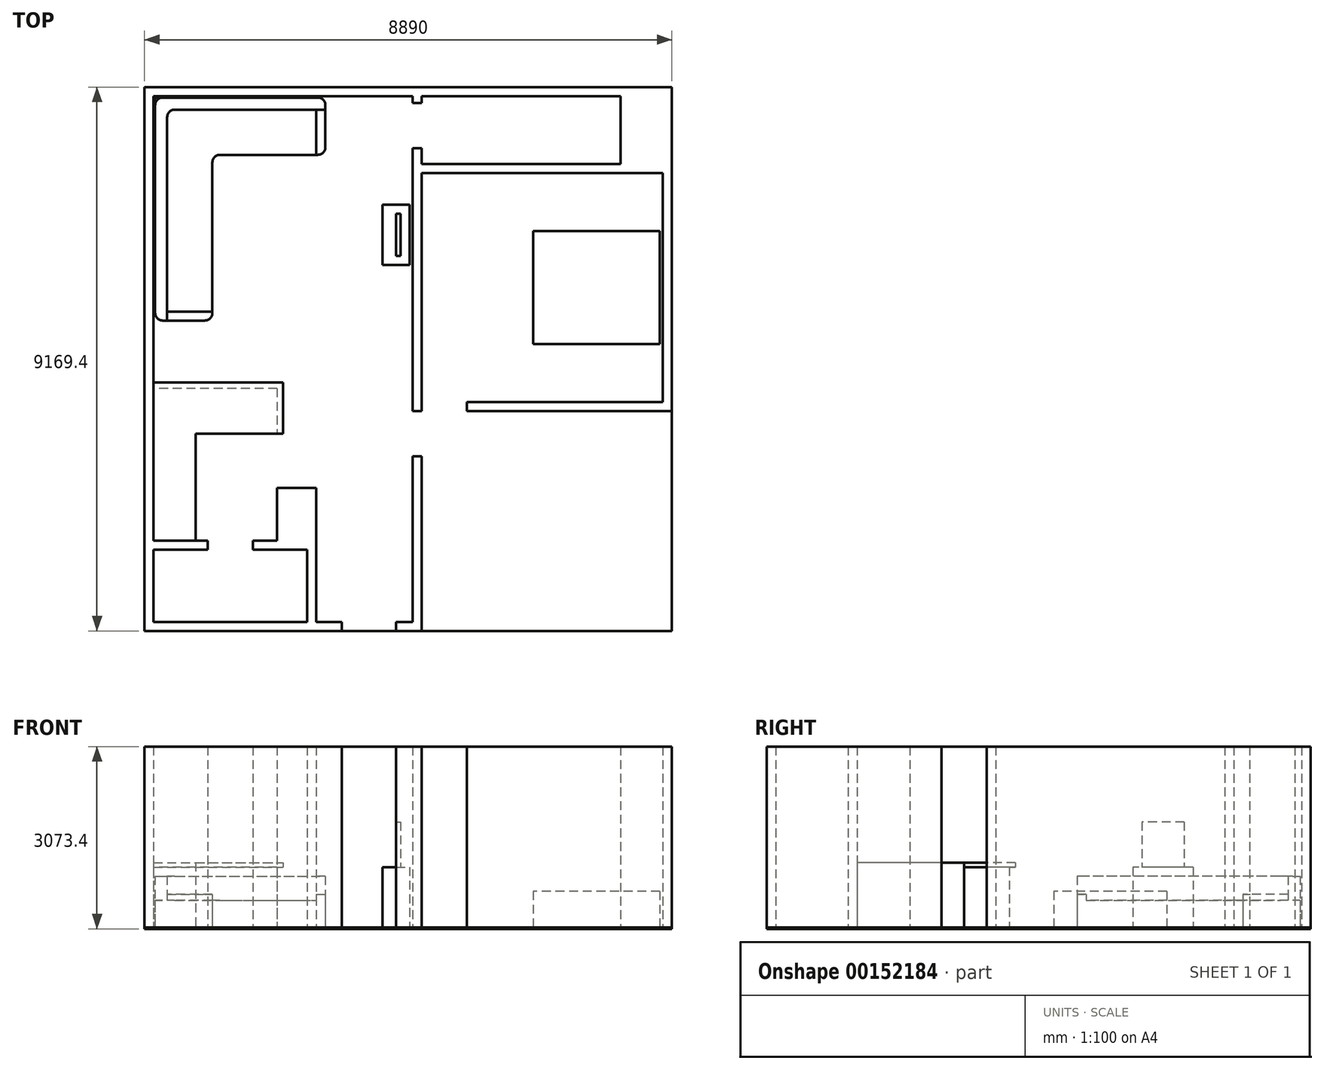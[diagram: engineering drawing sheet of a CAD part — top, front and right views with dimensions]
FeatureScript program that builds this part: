
annotation { "Feature Type Name" : "Feature", "Feature Type Description" : "" }
export const myFeature = defineFeature(function(context is Context, id is Id, definition is map)
    precondition{}
    {
        {
            var Q0;
            Q0=qCreatedBy(makeId("Top.planeOp"),FACE);
            var sketch = newSketch(context, id + "F0", { "sketchPlane" : qUnion([Q0])});
            skLineSegment(sketch, "E0.bottom", {"start": v(-4368.8, 4927.6) * mm, "end": v(0, 4927.6) * mm});
            skLineSegment(sketch, "E0.top", {"start": v(-3657.6, 0) * mm, "end": v(0, 0) * mm, "construction": true});
            skLineSegment(sketch, "E0.left", {"start": v(-4368.8, 4927.6) * mm, "end": v(-4368.8, 152.4) * mm});
            skLineSegment(sketch, "E0.right", {"start": v(0, 4927.6) * mm, "end": v(0, 4813.3) * mm});
            skLineSegment(sketch, "E1.bottom", {"start": v(-2286, 0) * mm, "end": v(-3657.6, 0) * mm});
            skLineSegment(sketch, "E1.top", {"start": v(152.4, 5080) * mm, "end": v(-4521.2, 5080) * mm});
            skLineSegment(sketch, "E1.left", {"start": v(152.4, 0) * mm, "end": v(152.4, 3632.2) * mm});
            skLineSegment(sketch, "E1.right", {"start": v(-4521.2, -6.75) * mm, "end": v(-4521.2, 5080) * mm});
            skLineSegment(sketch, "E2.bottom", {"start": v(-3657.6, 0) * mm, "end": v(-2286, 0) * mm});
            skLineSegment(sketch, "E2.top", {"start": v(-3657.6, -762) * mm, "end": v(-2286, -762) * mm});
            skLineSegment(sketch, "E2.left", {"start": v(-4368.8, 0) * mm, "end": v(-4368.8, -762) * mm});
            skLineSegment(sketch, "E2.right", {"start": v(-2286, 0) * mm, "end": v(-2286, -762) * mm});
            skLineSegment(sketch, "E3.top", {"start": v(-4368.8, -2565.4) * mm, "end": v(-3657.6, -2565.4) * mm});
            skLineSegment(sketch, "E3.left", {"start": v(-4368.8, 0) * mm, "end": v(-4368.8, -2565.4) * mm});
            skLineSegment(sketch, "E3.right", {"start": v(-3657.6, -762) * mm, "end": v(-3657.6, -2565.4) * mm});
            skLineSegment(sketch, "E4.bottom", {"start": v(-4368.8, -2565.4) * mm, "end": v(-3454.4, -2565.4) * mm});
            skLineSegment(sketch, "E4.top", {"start": v(-4368.8, -4089.4) * mm, "end": v(-1625.6, -4089.4) * mm});
            skLineSegment(sketch, "E4.left", {"start": v(-4368.8, -2717.8) * mm, "end": v(-4368.8, -3937) * mm});
            skLineSegment(sketch, "E4.right", {"start": v(-1625.6, -2565.4) * mm, "end": v(-1625.6, -3937) * mm});
            skLineSegment(sketch, "E5.1", {"start": v(-4368.8, -2717.8) * mm, "end": v(-3454.4, -2717.8) * mm});
            skLineSegment(sketch, "E5.2", {"start": v(-1778, -2717.8) * mm, "end": v(-1778, -3937) * mm});
            skLineSegment(sketch, "E5.3", {"start": v(-4368.8, -3937) * mm, "end": v(-1778, -3937) * mm});
            skLineSegment(sketch, "E6", {"start": v(-3073.4, -3937) * mm, "end": v(-3073.4, -3445.39) * mm, "construction": true});
            skLineSegment(sketch, "E7", {"start": v(-3454.4, -2565.4) * mm, "end": v(-3454.4, -2717.8) * mm});
            skLineSegment(sketch, "E8", {"start": v(-2692.4, -2717.8) * mm, "end": v(-2692.4, -2565.4) * mm});
            skLineSegment(sketch, "E9.0", {"start": v(-4521.2, -1866.2) * mm, "end": v(-4521.2, -4089.4) * mm});
            skLineSegment(sketch, "E9.1", {"start": v(-4521.2, 0) * mm, "end": v(-4521.2, -1866.2) * mm});
            skLineSegment(sketch, "E10", {"start": v(-4368.8, -4089.4) * mm, "end": v(-4521.2, -4089.4) * mm});
            skLineSegment(sketch, "E11.right", {"start": v(-2286, 0) * mm, "end": v(-2311.9, 0) * mm});
            skLineSegment(sketch, "E12.bottom", {"start": v(-1625.6, -4089.4) * mm, "end": v(-1193.8, -4089.4) * mm});
            skLineSegment(sketch, "E12.top", {"start": v(-1625.6, -3937) * mm, "end": v(-1193.8, -3937) * mm});
            skLineSegment(sketch, "E12.right", {"start": v(152.4, -4089.4) * mm, "end": v(152.4, -3937) * mm});
            skLineSegment(sketch, "E13.top", {"start": v(152.4, -1143) * mm, "end": v(0, -1143) * mm});
            skLineSegment(sketch, "E13.left", {"start": v(152.4, -3937) * mm, "end": v(152.4, -1143) * mm});
            skLineSegment(sketch, "E13.right", {"start": v(0, -3937) * mm, "end": v(0, -1143) * mm});
            skLineSegment(sketch, "E14.top", {"start": v(0, -381) * mm, "end": v(152.4, -381) * mm});
            skLineSegment(sketch, "E14.left", {"start": v(0, 0) * mm, "end": v(0, -381) * mm});
            skLineSegment(sketch, "E14.right", {"start": v(152.4, 0) * mm, "end": v(152.4, -381) * mm});
            skLineSegment(sketch, "E15.bottom", {"start": v(152.4, 5080) * mm, "end": v(3505.2, 5080) * mm});
            skLineSegment(sketch, "E15.top", {"start": v(152.4, 4927.6) * mm, "end": v(3505.2, 4927.6) * mm});
            skLineSegment(sketch, "E16.bottom", {"start": v(3505.2, 5080) * mm, "end": v(4368.8, 5080) * mm});
            skLineSegment(sketch, "E16.left", {"start": v(3505.2, 4927.6) * mm, "end": v(3505.2, 3784.6) * mm});
            skLineSegment(sketch, "E16.right", {"start": v(4368.8, 5080) * mm, "end": v(4368.8, 3784.6) * mm});
            skLineSegment(sketch, "E17.bottom", {"start": v(3505.2, 3784.6) * mm, "end": v(152.4, 3784.6) * mm});
            skLineSegment(sketch, "E17.top", {"start": v(4216.4, 3632.2) * mm, "end": v(152.4, 3632.2) * mm});
            skLineSegment(sketch, "E17.left", {"start": v(4368.8, 3784.6) * mm, "end": v(4368.8, 3632.2) * mm});
            skLineSegment(sketch, "E18.top", {"start": v(4368.8, -381) * mm, "end": v(4216.4, -381) * mm});
            skLineSegment(sketch, "E18.left", {"start": v(4368.8, 3632.2) * mm, "end": v(4368.8, -381) * mm});
            skLineSegment(sketch, "E18.right", {"start": v(4216.4, 3632.2) * mm, "end": v(4216.4, -228.6) * mm});
            skLineSegment(sketch, "E19.bottom", {"start": v(4216.4, -381) * mm, "end": v(914.4, -381) * mm});
            skLineSegment(sketch, "E19.top", {"start": v(4216.4, -228.6) * mm, "end": v(914.4, -228.6) * mm});
            skLineSegment(sketch, "E19.right", {"start": v(914.4, -381) * mm, "end": v(914.4, -228.6) * mm});
            skLineSegment(sketch, "E20.bottom", {"start": v(0, 4813.3) * mm, "end": v(152.4, 4813.3) * mm});
            skLineSegment(sketch, "E20.top", {"start": v(0, 4051.3) * mm, "end": v(152.4, 4051.3) * mm});
            skLineSegment(sketch, "E21", {"start": v(3505.2, 4432.3) * mm, "end": v(2543.45, 4432.3) * mm, "construction": true});
            skLineSegment(sketch, "E22.trimOffspring", {"start": v(152.4, 3784.6) * mm, "end": v(152.4, 4051.3) * mm});
            skLineSegment(sketch, "E23.trimOffspring", {"start": v(152.4, 4813.3) * mm, "end": v(152.4, 4927.6) * mm});
            skLineSegment(sketch, "E24.trimOffspring", {"start": v(0, 4051.3) * mm, "end": v(0, 0) * mm});
            skLineSegment(sketch, "E25", {"start": v(-4368.8, 0) * mm, "end": v(-3657.6, 0) * mm});
            skLineSegment(sketch, "E26", {"start": v(-4368.8, 0) * mm, "end": v(-4368.8, 152.4) * mm});
            skLineSegment(sketch, "E27.trimOffspring", {"start": v(-2692.4, -2565.4) * mm, "end": v(-2286, -2565.4) * mm});
            skLineSegment(sketch, "E28.trimOffspring", {"start": v(-2692.4, -2717.8) * mm, "end": v(-1778, -2717.8) * mm});
            skLineSegment(sketch, "E29", {"start": v(-736.6, -4089.4) * mm, "end": v(-736.6, -3937) * mm, "construction": true});
            skLineSegment(sketch, "E30.left", {"start": v(-1193.8, -4089.4) * mm, "end": v(-1193.8, -3937) * mm});
            skLineSegment(sketch, "E30.right", {"start": v(-279.4, -4089.4) * mm, "end": v(-279.4, -3937) * mm});
            skLineSegment(sketch, "E31.trimOffspring", {"start": v(-279.4, -4089.4) * mm, "end": v(152.4, -4089.4) * mm});
            skLineSegment(sketch, "E32.trimOffspring", {"start": v(-279.4, -3937) * mm, "end": v(0, -3937) * mm});
            skLineSegment(sketch, "E33.top", {"start": v(-1625.6, -1676.4) * mm, "end": v(-2286, -1676.4) * mm});
            skLineSegment(sketch, "E33.left", {"start": v(-1625.6, -2565.4) * mm, "end": v(-1625.6, -1676.4) * mm});
            skLineSegment(sketch, "E33.right", {"start": v(-2286, -2565.4) * mm, "end": v(-2286, -1676.4) * mm});
            skSolve(sketch);
        }
        {
            var Q0;
            Q0 = qSketchRegion(id + "F0", true);
            extrude(context, id + "F1", {"entities" : qUnion([Q0]), "depth" : 1016 * mm});
        }
        {
            var Q0;
            Q0=makeQuery(id+"F1.opExtrude","CAP_FACE",FACE,{"disambiguationData":[OSD([sQuery(id+"F0.wireOp",EDGE,"E0.bottom"),sQuery(id+"F0.wireOp",EDGE,"E0.left"),sQuery(id+"F0.wireOp",EDGE,"E0.right"),sQuery(id+"F0.wireOp",EDGE,"E1.top"),sQuery(id+"F0.wireOp",EDGE,"E1.left"),sQuery(id+"F0.wireOp",EDGE,"E1.right"),sQuery(id+"F0.wireOp",EDGE,"E2.top"),sQuery(id+"F0.wireOp",EDGE,"E2.right"),sQuery(id+"F0.wireOp",EDGE,"E3.right"),sQuery(id+"F0.wireOp",EDGE,"E4.bottom"),sQuery(id+"F0.wireOp",EDGE,"E4.top"),sQuery(id+"F0.wireOp",EDGE,"E4.left"),sQuery(id+"F0.wireOp",EDGE,"E4.right"),sQuery(id+"F0.wireOp",EDGE,"E5.1"),sQuery(id+"F0.wireOp",EDGE,"E5.2"),sQuery(id+"F0.wireOp",EDGE,"E5.3"),sQuery(id+"F0.wireOp",EDGE,"E7"),sQuery(id+"F0.wireOp",EDGE,"E8"),sQuery(id+"F0.wireOp",EDGE,"E9.0"),sQuery(id+"F0.wireOp",EDGE,"E9.1"),sQuery(id+"F0.wireOp",EDGE,"E10"),sQuery(id+"F0.wireOp",EDGE,"E12.bottom"),sQuery(id+"F0.wireOp",EDGE,"E12.top"),sQuery(id+"F0.wireOp",EDGE,"E14.top"),sQuery(id+"F0.wireOp",EDGE,"E14.left"),sQuery(id+"F0.wireOp",EDGE,"E14.right"),sQuery(id+"F0.wireOp",EDGE,"E15.bottom"),sQuery(id+"F0.wireOp",EDGE,"E15.top"),sQuery(id+"F0.wireOp",EDGE,"E16.bottom"),sQuery(id+"F0.wireOp",EDGE,"E16.left"),sQuery(id+"F0.wireOp",EDGE,"E16.right"),sQuery(id+"F0.wireOp",EDGE,"E17.bottom"),sQuery(id+"F0.wireOp",EDGE,"E17.top"),sQuery(id+"F0.wireOp",EDGE,"E17.left"),sQuery(id+"F0.wireOp",EDGE,"E18.top"),sQuery(id+"F0.wireOp",EDGE,"E18.left"),sQuery(id+"F0.wireOp",EDGE,"E18.right"),sQuery(id+"F0.wireOp",EDGE,"E19.bottom"),sQuery(id+"F0.wireOp",EDGE,"E19.top"),sQuery(id+"F0.wireOp",EDGE,"E19.right"),sQuery(id+"F0.wireOp",EDGE,"E20.bottom"),sQuery(id+"F0.wireOp",EDGE,"E20.top"),sQuery(id+"F0.wireOp",EDGE,"E22.trimOffspring"),sQuery(id+"F0.wireOp",EDGE,"E23.trimOffspring"),sQuery(id+"F0.wireOp",EDGE,"E24.trimOffspring"),sQuery(id+"F0.wireOp",EDGE,"E1.bottom"),sQuery(id+"F0.wireOp",EDGE,"E25"),sQuery(id+"F0.wireOp",EDGE,"E26"),sQuery(id+"F0.wireOp",EDGE,"E27.trimOffspring"),sQuery(id+"F0.wireOp",EDGE,"E28.trimOffspring"),sQuery(id+"F0.wireOp",EDGE,"E30.left"),sQuery(id+"F0.wireOp",EDGE,"E33.top"),sQuery(id+"F0.wireOp",EDGE,"E33.left"),sQuery(id+"F0.wireOp",EDGE,"E33.right")])],"isStart":false});
            var sketch = newSketch(context, id + "F2", { "sketchPlane" : qUnion([Q0])});
            skLineSegment(sketch, "E34.0", {"start": v(-2286, 0) * mm, "end": v(-2286, -762) * mm});
            skLineSegment(sketch, "E34.1", {"start": v(-3657.6, -762) * mm, "end": v(-2286, -762) * mm});
            skLineSegment(sketch, "E34.2", {"start": v(-3657.6, -762) * mm, "end": v(-3657.6, -2565.4) * mm});
            skLineSegment(sketch, "E35.0", {"start": v(-3657.6, -2565.4) * mm, "end": v(-3454.4, -2565.4) * mm});
            skLineSegment(sketch, "E35.1", {"start": v(-1625.6, -1676.4) * mm, "end": v(-1625.6, -3937) * mm});
            skLineSegment(sketch, "E35.2", {"start": v(-1625.6, -1676.4) * mm, "end": v(-2286, -1676.4) * mm});
            skLineSegment(sketch, "E35.3", {"start": v(-2286, -2565.4) * mm, "end": v(-2286, -1676.4) * mm});
            skLineSegment(sketch, "E35.4", {"start": v(-2692.4, -2565.4) * mm, "end": v(-2286, -2565.4) * mm});
            skLineSegment(sketch, "E35.5", {"start": v(-2692.4, -2717.8) * mm, "end": v(-1778, -2717.8) * mm});
            skLineSegment(sketch, "E35.6", {"start": v(-1778, -2717.8) * mm, "end": v(-1778, -3937) * mm});
            skLineSegment(sketch, "E35.7", {"start": v(-4368.8, -3937) * mm, "end": v(-1778, -3937) * mm});
            skLineSegment(sketch, "E35.8", {"start": v(-1625.6, -3937) * mm, "end": v(-1193.8, -3937) * mm});
            skLineSegment(sketch, "E35.9", {"start": v(-1193.8, -4089.4) * mm, "end": v(-4521.2, -4089.4) * mm});
            skLineSegment(sketch, "E35.10", {"start": v(-4368.8, -2717.8) * mm, "end": v(-4368.8, -3937) * mm});
            skLineSegment(sketch, "E35.11", {"start": v(-4521.2, -4089.4) * mm, "end": v(-4521.2, 5080) * mm});
            skLineSegment(sketch, "E35.12", {"start": v(-4368.8, -2717.8) * mm, "end": v(-3454.4, -2717.8) * mm});
            skLineSegment(sketch, "E35.13", {"start": v(-4368.8, 4927.6) * mm, "end": v(-4368.8, 101.6) * mm});
            skLineSegment(sketch, "E35.14", {"start": v(0, -3937) * mm, "end": v(0, -1143) * mm});
            skLineSegment(sketch, "E35.15", {"start": v(152.4, -4089.4) * mm, "end": v(152.4, -1143) * mm});
            skLineSegment(sketch, "E35.16", {"start": v(-279.4, -4089.4) * mm, "end": v(152.4, -4089.4) * mm});
            skLineSegment(sketch, "E35.17", {"start": v(-279.4, -3937) * mm, "end": v(0, -3937) * mm});
            skLineSegment(sketch, "E35.18", {"start": v(152.4, 3632.2) * mm, "end": v(152.4, -381) * mm});
            skLineSegment(sketch, "E35.19", {"start": v(0, 4051.3) * mm, "end": v(0, -381) * mm});
            skLineSegment(sketch, "E35.20", {"start": v(4368.8, -381) * mm, "end": v(914.4, -381) * mm});
            skLineSegment(sketch, "E35.21", {"start": v(4216.4, -228.6) * mm, "end": v(914.4, -228.6) * mm});
            skLineSegment(sketch, "E35.22", {"start": v(914.4, -381) * mm, "end": v(914.4, -228.6) * mm});
            skLineSegment(sketch, "E35.23", {"start": v(0, -381) * mm, "end": v(152.4, -381) * mm});
            skLineSegment(sketch, "E35.24", {"start": v(152.4, -1143) * mm, "end": v(0, -1143) * mm});
            skLineSegment(sketch, "E35.25", {"start": v(-279.4, -4089.4) * mm, "end": v(-279.4, -3937) * mm});
            skLineSegment(sketch, "E35.26", {"start": v(-1193.8, -4089.4) * mm, "end": v(-1193.8, -3937) * mm});
            skLineSegment(sketch, "E35.27", {"start": v(-2692.4, -2717.8) * mm, "end": v(-2692.4, -2565.4) * mm});
            skLineSegment(sketch, "E35.28", {"start": v(-3454.4, -2565.4) * mm, "end": v(-3454.4, -2717.8) * mm});
            skLineSegment(sketch, "E35.29", {"start": v(-4521.2, 5080) * mm, "end": v(4368.8, 5080) * mm});
            skLineSegment(sketch, "E35.30", {"start": v(-4368.8, 4927.6) * mm, "end": v(0, 4927.6) * mm});
            skLineSegment(sketch, "E35.31", {"start": v(4368.8, 5080) * mm, "end": v(4368.8, -381) * mm});
            skLineSegment(sketch, "E35.32", {"start": v(3505.2, 4927.6) * mm, "end": v(3505.2, 3784.6) * mm});
            skLineSegment(sketch, "E35.33", {"start": v(4216.4, 3632.2) * mm, "end": v(152.4, 3632.2) * mm});
            skLineSegment(sketch, "E35.34", {"start": v(4216.4, 3632.2) * mm, "end": v(4216.4, -228.6) * mm});
            skLineSegment(sketch, "E35.35", {"start": v(3505.2, 3784.6) * mm, "end": v(152.4, 3784.6) * mm});
            skLineSegment(sketch, "E35.36", {"start": v(152.4, 3784.6) * mm, "end": v(152.4, 4051.3) * mm});
            skLineSegment(sketch, "E35.37", {"start": v(0, 4051.3) * mm, "end": v(152.4, 4051.3) * mm});
            skLineSegment(sketch, "E35.38", {"start": v(0, 4813.3) * mm, "end": v(152.4, 4813.3) * mm});
            skLineSegment(sketch, "E35.39", {"start": v(152.4, 4813.3) * mm, "end": v(152.4, 4927.6) * mm});
            skLineSegment(sketch, "E35.40", {"start": v(0, 4927.6) * mm, "end": v(0, 4813.3) * mm});
            skLineSegment(sketch, "E35.41", {"start": v(152.4, 4927.6) * mm, "end": v(3505.2, 4927.6) * mm});
            skLineSegment(sketch, "E36", {"start": v(-2286, 101.6) * mm, "end": v(-4368.8, 101.6) * mm});
            skPoint(sketch, "E37.orphan", {"position": v(-4368.8, 0) * mm});
            skLineSegment(sketch, "E38.bottom", {"start": v(-2286, 101.6) * mm, "end": v(-2184.4, 101.6) * mm});
            skLineSegment(sketch, "E38.top", {"start": v(-2286, -762) * mm, "end": v(-2184.4, -762) * mm});
            skLineSegment(sketch, "E38.right", {"start": v(-2184.4, 101.6) * mm, "end": v(-2184.4, -762) * mm});
            skSolve(sketch);
        }
        {
            var Q0;
            Q0=makeQuery(id+"F2.imprint","IMPRINT",FACE,{"disambiguationData":[TD([[makeQuery(id+"F2.imprint","IMPRINT",EDGE,{"derivedFrom":sQuery(id+"F2.wireOp",EDGE,"E34.1")}),1.0]])]});
            var Q1;
            Q1=makeQuery(id+"F2.imprint","IMPRINT",FACE,{"disambiguationData":[TD([[makeQuery(id+"F2.imprint","IMPRINT",EDGE,{"derivedFrom":sQuery(id+"F2.wireOp",EDGE,"E35.14")}),-1.0]])]});
            var Q2;
            {var subQ0=sQuery(id+"F2.wireOp",EDGE,"E36");Q2=makeQuery(id+"F2.imprint","IMPRINT",FACE,{"disambiguationData":[TD([[makeQuery(id+"F2.imprint","IMPRINT",EDGE,{"derivedFrom":subQ0}),1.0]])]});}
            extrude(context, id + "F3", {"entities" : qUnion([Q0, Q1, Q2]), "operationType" : NewBodyOperationType.ADD, "depth" : 76.2 * mm});
        }
        {
            var Q0;
            Q0=makeQuery(id+"F3.opExtrude","CAP_FACE",FACE,{"disambiguationData":[OSD([sQuery(id+"F2.wireOp",EDGE,"E34.1"),sQuery(id+"F2.wireOp",EDGE,"E34.2"),sQuery(id+"F2.wireOp",EDGE,"E35.0"),sQuery(id+"F2.wireOp",EDGE,"E35.1"),sQuery(id+"F2.wireOp",EDGE,"E35.2"),sQuery(id+"F2.wireOp",EDGE,"E35.3"),sQuery(id+"F2.wireOp",EDGE,"E35.4"),sQuery(id+"F2.wireOp",EDGE,"E35.5"),sQuery(id+"F2.wireOp",EDGE,"E35.6"),sQuery(id+"F2.wireOp",EDGE,"E35.7"),sQuery(id+"F2.wireOp",EDGE,"E35.8"),sQuery(id+"F2.wireOp",EDGE,"E35.9"),sQuery(id+"F2.wireOp",EDGE,"E35.10"),sQuery(id+"F2.wireOp",EDGE,"E35.11"),sQuery(id+"F2.wireOp",EDGE,"E35.12"),sQuery(id+"F2.wireOp",EDGE,"E35.13"),sQuery(id+"F2.wireOp",EDGE,"E35.18"),sQuery(id+"F2.wireOp",EDGE,"E35.19"),sQuery(id+"F2.wireOp",EDGE,"E35.20"),sQuery(id+"F2.wireOp",EDGE,"E35.21"),sQuery(id+"F2.wireOp",EDGE,"E35.22"),sQuery(id+"F2.wireOp",EDGE,"E35.23"),sQuery(id+"F2.wireOp",EDGE,"E35.26"),sQuery(id+"F2.wireOp",EDGE,"E35.27"),sQuery(id+"F2.wireOp",EDGE,"E35.28"),sQuery(id+"F2.wireOp",EDGE,"E35.29"),sQuery(id+"F2.wireOp",EDGE,"E35.30"),sQuery(id+"F2.wireOp",EDGE,"E35.31"),sQuery(id+"F2.wireOp",EDGE,"E35.32"),sQuery(id+"F2.wireOp",EDGE,"E35.33"),sQuery(id+"F2.wireOp",EDGE,"E35.34"),sQuery(id+"F2.wireOp",EDGE,"E35.35"),sQuery(id+"F2.wireOp",EDGE,"E35.36"),sQuery(id+"F2.wireOp",EDGE,"E35.37"),sQuery(id+"F2.wireOp",EDGE,"E35.38"),sQuery(id+"F2.wireOp",EDGE,"E35.39"),sQuery(id+"F2.wireOp",EDGE,"E35.40"),sQuery(id+"F2.wireOp",EDGE,"E35.41"),sQuery(id+"F2.wireOp",EDGE,"E36"),sQuery(id+"F2.wireOp",EDGE,"E38.bottom"),sQuery(id+"F2.wireOp",EDGE,"E38.top"),sQuery(id+"F2.wireOp",EDGE,"E38.right")])],"isStart":false});
            var sketch = newSketch(context, id + "F4", { "sketchPlane" : qUnion([Q0])});
            skLineSegment(sketch, "E39.3", {"start": v(-3657.6, -2565.4) * mm, "end": v(-3454.4, -2565.4) * mm});
            skLineSegment(sketch, "E39.4", {"start": v(-1625.6, -1676.4) * mm, "end": v(-1625.6, -3937) * mm});
            skLineSegment(sketch, "E39.5", {"start": v(-1625.6, -1676.4) * mm, "end": v(-2286, -1676.4) * mm});
            skLineSegment(sketch, "E39.6", {"start": v(-2286, -2565.4) * mm, "end": v(-2286, -1676.4) * mm});
            skLineSegment(sketch, "E39.7", {"start": v(-2692.4, -2565.4) * mm, "end": v(-2286, -2565.4) * mm});
            skLineSegment(sketch, "E39.8", {"start": v(-2692.4, -2717.8) * mm, "end": v(-1778, -2717.8) * mm});
            skLineSegment(sketch, "E39.9", {"start": v(-1778, -2717.8) * mm, "end": v(-1778, -3937) * mm});
            skLineSegment(sketch, "E39.10", {"start": v(-4368.8, -3937) * mm, "end": v(-1778, -3937) * mm});
            skLineSegment(sketch, "E39.11", {"start": v(-1625.6, -3937) * mm, "end": v(-1193.8, -3937) * mm});
            skLineSegment(sketch, "E39.12", {"start": v(-1193.8, -4089.4) * mm, "end": v(-4521.2, -4089.4) * mm});
            skLineSegment(sketch, "E39.13", {"start": v(-4368.8, -2717.8) * mm, "end": v(-4368.8, -3937) * mm});
            skLineSegment(sketch, "E39.14", {"start": v(-4521.2, -4089.4) * mm, "end": v(-4521.2, 5080) * mm});
            skLineSegment(sketch, "E39.15", {"start": v(-4368.8, -2717.8) * mm, "end": v(-3454.4, -2717.8) * mm});
            skLineSegment(sketch, "E39.16", {"start": v(-4368.8, 4927.6) * mm, "end": v(-4368.8, 101.6) * mm});
            skLineSegment(sketch, "E39.17", {"start": v(0, -3937) * mm, "end": v(0, -1143) * mm});
            skLineSegment(sketch, "E39.18", {"start": v(152.4, -4089.4) * mm, "end": v(152.4, -1143) * mm});
            skLineSegment(sketch, "E39.19", {"start": v(-279.4, -4089.4) * mm, "end": v(152.4, -4089.4) * mm});
            skLineSegment(sketch, "E39.20", {"start": v(-279.4, -3937) * mm, "end": v(0, -3937) * mm});
            skLineSegment(sketch, "E39.21", {"start": v(152.4, 3632.2) * mm, "end": v(152.4, -381) * mm});
            skLineSegment(sketch, "E39.22", {"start": v(0, 4051.3) * mm, "end": v(0, -381) * mm});
            skLineSegment(sketch, "E39.23", {"start": v(4368.8, -381) * mm, "end": v(914.4, -381) * mm});
            skLineSegment(sketch, "E39.24", {"start": v(4216.4, -228.6) * mm, "end": v(914.4, -228.6) * mm});
            skLineSegment(sketch, "E39.25", {"start": v(914.4, -381) * mm, "end": v(914.4, -228.6) * mm});
            skLineSegment(sketch, "E39.26", {"start": v(0, -381) * mm, "end": v(152.4, -381) * mm});
            skLineSegment(sketch, "E39.27", {"start": v(152.4, -1143) * mm, "end": v(0, -1143) * mm});
            skLineSegment(sketch, "E39.28", {"start": v(-279.4, -4089.4) * mm, "end": v(-279.4, -3937) * mm});
            skLineSegment(sketch, "E39.29", {"start": v(-1193.8, -4089.4) * mm, "end": v(-1193.8, -3937) * mm});
            skLineSegment(sketch, "E39.30", {"start": v(-2692.4, -2717.8) * mm, "end": v(-2692.4, -2565.4) * mm});
            skLineSegment(sketch, "E39.31", {"start": v(-3454.4, -2565.4) * mm, "end": v(-3454.4, -2717.8) * mm});
            skLineSegment(sketch, "E39.32", {"start": v(-4521.2, 5080) * mm, "end": v(4368.8, 5080) * mm});
            skLineSegment(sketch, "E39.33", {"start": v(-4368.8, 4927.6) * mm, "end": v(0, 4927.6) * mm});
            skLineSegment(sketch, "E39.34", {"start": v(4368.8, 5080) * mm, "end": v(4368.8, -381) * mm});
            skLineSegment(sketch, "E39.35", {"start": v(3505.2, 4927.6) * mm, "end": v(3505.2, 3784.6) * mm});
            skLineSegment(sketch, "E39.36", {"start": v(4216.4, 3632.2) * mm, "end": v(152.4, 3632.2) * mm});
            skLineSegment(sketch, "E39.37", {"start": v(4216.4, 3632.2) * mm, "end": v(4216.4, -228.6) * mm});
            skLineSegment(sketch, "E39.38", {"start": v(3505.2, 3784.6) * mm, "end": v(152.4, 3784.6) * mm});
            skLineSegment(sketch, "E39.39", {"start": v(152.4, 3784.6) * mm, "end": v(152.4, 4051.3) * mm});
            skLineSegment(sketch, "E39.40", {"start": v(0, 4051.3) * mm, "end": v(152.4, 4051.3) * mm});
            skLineSegment(sketch, "E39.41", {"start": v(0, 4813.3) * mm, "end": v(152.4, 4813.3) * mm});
            skLineSegment(sketch, "E39.42", {"start": v(152.4, 4813.3) * mm, "end": v(152.4, 4927.6) * mm});
            skLineSegment(sketch, "E39.43", {"start": v(0, 4927.6) * mm, "end": v(0, 4813.3) * mm});
            skLineSegment(sketch, "E39.44", {"start": v(152.4, 4927.6) * mm, "end": v(3505.2, 4927.6) * mm});
            skPoint(sketch, "E39.46", {"position": v(-4368.8, 0) * mm});
            skLineSegment(sketch, "E40", {"start": v(-4368.8, 101.6) * mm, "end": v(-4368.8, -2565.4) * mm});
            skPoint(sketch, "E39.45.end.orphan", {"position": v(-4368.8, 101.6) * mm});
            skPoint(sketch, "E39.2.end.orphan", {"position": v(-3657.6, -2565.4) * mm});
            skLineSegment(sketch, "E41", {"start": v(-3657.6, -2565.4) * mm, "end": v(-4368.8, -2565.4) * mm});
            skSolve(sketch);
        }
        {
            var Q0;
            Q0=makeQuery(id+"F4.imprint","IMPRINT",FACE,{"disambiguationData":[TD([[makeQuery(id+"F4.imprint","IMPRINT",EDGE,{"derivedFrom":sQuery(id+"F4.wireOp",EDGE,"E39.17")}),-1.0]])]});
            var Q1;
            Q1=makeQuery(id+"F4.imprint","IMPRINT",FACE,{"disambiguationData":[TD([[makeQuery(id+"F4.imprint","IMPRINT",EDGE,{"derivedFrom":sQuery(id+"F4.wireOp",EDGE,"E39.3")}),-1.0]])]});
            extrude(context, id + "F5", {"entities" : qUnion([Q0, Q1]), "operationType" : NewBodyOperationType.ADD, "depth" : 1955.8 * mm});
        }
        {
            var Q0;
            Q0=makeQuery(id+"F1.opExtrude","CAP_FACE",FACE,{"disambiguationData":[OSD([sQuery(id+"F0.wireOp",EDGE,"E0.bottom"),sQuery(id+"F0.wireOp",EDGE,"E0.left"),sQuery(id+"F0.wireOp",EDGE,"E0.right"),sQuery(id+"F0.wireOp",EDGE,"E1.top"),sQuery(id+"F0.wireOp",EDGE,"E1.left"),sQuery(id+"F0.wireOp",EDGE,"E1.right"),sQuery(id+"F0.wireOp",EDGE,"E2.top"),sQuery(id+"F0.wireOp",EDGE,"E2.right"),sQuery(id+"F0.wireOp",EDGE,"E3.right"),sQuery(id+"F0.wireOp",EDGE,"E4.bottom"),sQuery(id+"F0.wireOp",EDGE,"E4.top"),sQuery(id+"F0.wireOp",EDGE,"E4.left"),sQuery(id+"F0.wireOp",EDGE,"E4.right"),sQuery(id+"F0.wireOp",EDGE,"E5.1"),sQuery(id+"F0.wireOp",EDGE,"E5.2"),sQuery(id+"F0.wireOp",EDGE,"E5.3"),sQuery(id+"F0.wireOp",EDGE,"E7"),sQuery(id+"F0.wireOp",EDGE,"E8"),sQuery(id+"F0.wireOp",EDGE,"E9.0"),sQuery(id+"F0.wireOp",EDGE,"E9.1"),sQuery(id+"F0.wireOp",EDGE,"E10"),sQuery(id+"F0.wireOp",EDGE,"E12.bottom"),sQuery(id+"F0.wireOp",EDGE,"E12.top"),sQuery(id+"F0.wireOp",EDGE,"E14.top"),sQuery(id+"F0.wireOp",EDGE,"E14.left"),sQuery(id+"F0.wireOp",EDGE,"E14.right"),sQuery(id+"F0.wireOp",EDGE,"E15.bottom"),sQuery(id+"F0.wireOp",EDGE,"E15.top"),sQuery(id+"F0.wireOp",EDGE,"E16.bottom"),sQuery(id+"F0.wireOp",EDGE,"E16.left"),sQuery(id+"F0.wireOp",EDGE,"E16.right"),sQuery(id+"F0.wireOp",EDGE,"E17.bottom"),sQuery(id+"F0.wireOp",EDGE,"E17.top"),sQuery(id+"F0.wireOp",EDGE,"E17.left"),sQuery(id+"F0.wireOp",EDGE,"E18.top"),sQuery(id+"F0.wireOp",EDGE,"E18.left"),sQuery(id+"F0.wireOp",EDGE,"E18.right"),sQuery(id+"F0.wireOp",EDGE,"E19.bottom"),sQuery(id+"F0.wireOp",EDGE,"E19.top"),sQuery(id+"F0.wireOp",EDGE,"E19.right"),sQuery(id+"F0.wireOp",EDGE,"E20.bottom"),sQuery(id+"F0.wireOp",EDGE,"E20.top"),sQuery(id+"F0.wireOp",EDGE,"E22.trimOffspring"),sQuery(id+"F0.wireOp",EDGE,"E23.trimOffspring"),sQuery(id+"F0.wireOp",EDGE,"E24.trimOffspring"),sQuery(id+"F0.wireOp",EDGE,"E1.bottom"),sQuery(id+"F0.wireOp",EDGE,"E25"),sQuery(id+"F0.wireOp",EDGE,"E26"),sQuery(id+"F0.wireOp",EDGE,"E27.trimOffspring"),sQuery(id+"F0.wireOp",EDGE,"E28.trimOffspring"),sQuery(id+"F0.wireOp",EDGE,"E30.left"),sQuery(id+"F0.wireOp",EDGE,"E33.top"),sQuery(id+"F0.wireOp",EDGE,"E33.left"),sQuery(id+"F0.wireOp",EDGE,"E33.right")])],"isStart":true});
            var sketch = newSketch(context, id + "F6", { "sketchPlane" : qUnion([Q0])});
            skLineSegment(sketch, "E42.bottom", {"start": v(-4521.2, 4089.4) * mm, "end": v(4368.8, 4089.4) * mm});
            skLineSegment(sketch, "E42.top", {"start": v(-4521.2, -5080) * mm, "end": v(4368.8, -5080) * mm});
            skLineSegment(sketch, "E42.left", {"start": v(-4521.2, 4089.4) * mm, "end": v(-4521.2, -5080) * mm});
            skLineSegment(sketch, "E42.right", {"start": v(4368.8, 4089.4) * mm, "end": v(4368.8, -5080) * mm});
            skSolve(sketch);
        }
        {
            var Q0;
            Q0 = qSketchRegion(id + "F6", true);
            extrude(context, id + "F7", {"entities" : qUnion([Q0]), "depth" : 25.4 * mm});
        }
        {
            var Q0;
            Q0=makeQuery(id+"F7.opExtrude","CAP_FACE",FACE,{"disambiguationData":[OSD([sQuery(id+"F6.wireOp",EDGE,"E42.bottom"),sQuery(id+"F6.wireOp",EDGE,"E42.top"),sQuery(id+"F6.wireOp",EDGE,"E42.left"),sQuery(id+"F6.wireOp",EDGE,"E42.right")])],"isStart":true});
            var sketch = newSketch(context, id + "F8", { "sketchPlane" : qUnion([Q0])});
            skLineSegment(sketch, "E43.bottom", {"start": v(-4343.4, 4902.2) * mm, "end": v(-1600.2, 4902.2) * mm});
            skLineSegment(sketch, "E43.top", {"start": v(-3251.2, 3937) * mm, "end": v(-1600.2, 3937) * mm});
            skLineSegment(sketch, "E43.left", {"start": v(-4343.4, 4902.2) * mm, "end": v(-4343.4, 3937) * mm});
            skLineSegment(sketch, "E43.right", {"start": v(-1473.2, 4775.2) * mm, "end": v(-1473.2, 4064) * mm});
            skLineSegment(sketch, "E44.bottom", {"start": v(-4216.4, 4902.2) * mm, "end": v(-3378.2, 4902.2) * mm});
            skLineSegment(sketch, "E44.top", {"start": v(-4216.4, 1143) * mm, "end": v(-3505.2, 1143) * mm});
            skLineSegment(sketch, "E44.left", {"start": v(-4343.4, 4775.2) * mm, "end": v(-4343.4, 1270) * mm});
            skLineSegment(sketch, "E44.right", {"start": v(-3378.2, 3810) * mm, "end": v(-3378.2, 1270) * mm});
            skPoint(sketch, "E45.visualSharp", {"position": v(-4343.4, 4902.2) * mm});
            skArc(sketch, "E45.filletArc", {"start": v(-4216.4, 4902.2) * mm, "mid": v(-4306.2, 4865) * mm, "end": v(-4343.4, 4775.2) * mm});
            skPoint(sketch, "E46.visualSharp", {"position": v(-3378.2, 3937) * mm});
            skArc(sketch, "E46.filletArc", {"start": v(-3251.2, 3937) * mm, "mid": v(-3341, 3899.8) * mm, "end": v(-3378.2, 3810) * mm});
            skPoint(sketch, "E47.visualSharp", {"position": v(-1473.2, 3937) * mm});
            skArc(sketch, "E47.filletArc", {"start": v(-1600.2, 3937) * mm, "mid": v(-1510.4, 3974.2) * mm, "end": v(-1473.2, 4064) * mm});
            skPoint(sketch, "E48.visualSharp", {"position": v(-1473.2, 4902.2) * mm});
            skArc(sketch, "E48.filletArc", {"start": v(-1473.2, 4775.2) * mm, "mid": v(-1510.4, 4865) * mm, "end": v(-1600.2, 4902.2) * mm});
            skPoint(sketch, "E49.visualSharp", {"position": v(-3378.2, 1143) * mm});
            skArc(sketch, "E49.filletArc", {"start": v(-3505.2, 1143) * mm, "mid": v(-3415.4, 1180.2) * mm, "end": v(-3378.2, 1270) * mm});
            skPoint(sketch, "E50.visualSharp", {"position": v(-4343.4, 1143) * mm});
            skArc(sketch, "E50.filletArc", {"start": v(-4343.4, 1270) * mm, "mid": v(-4306.2, 1180.2) * mm, "end": v(-4216.4, 1143) * mm});
            skSolve(sketch);
        }
        {
            var Q0;
            Q0 = qSketchRegion(id + "F8", true);
            extrude(context, id + "F9", {"entities" : qUnion([Q0]), "depth" : 457.2 * mm});
        }
        {
            var Q0;
            Q0=makeQuery(id+"F9.opExtrude","CAP_FACE",FACE,{"disambiguationData":[OSD([sQuery(id+"F8.wireOp",EDGE,"E43.bottom"),sQuery(id+"F8.wireOp",EDGE,"E43.top"),sQuery(id+"F8.wireOp",EDGE,"E43.left"),sQuery(id+"F8.wireOp",EDGE,"E43.right"),sQuery(id+"F8.wireOp",EDGE,"E44.bottom"),sQuery(id+"F8.wireOp",EDGE,"E44.top"),sQuery(id+"F8.wireOp",EDGE,"E44.left"),sQuery(id+"F8.wireOp",EDGE,"E44.right"),sQuery(id+"F8.wireOp",EDGE,"E46.filletArc"),sQuery(id+"F8.wireOp",EDGE,"E47.filletArc"),sQuery(id+"F8.wireOp",EDGE,"E48.filletArc"),sQuery(id+"F8.wireOp",EDGE,"E49.filletArc"),sQuery(id+"F8.wireOp",EDGE,"E50.filletArc")])],"isStart":false});
            var sketch = newSketch(context, id + "F10", { "sketchPlane" : qUnion([Q0])});
            skLineSegment(sketch, "E51.0", {"start": v(-4216.4, 4902.2) * mm, "end": v(-1600.2, 4902.2) * mm});
            skLineSegment(sketch, "E51.1", {"start": v(-4343.4, 4775.2) * mm, "end": v(-4343.4, 1270) * mm});
            skLineSegment(sketch, "E51.2", {"start": v(-4216.4, 1143) * mm, "end": v(-3505.2, 1143) * mm});
            skArc(sketch, "E51.3", {"start": v(-4343.4, 1270) * mm, "mid": v(-4306.2, 1180.2) * mm, "end": v(-4216.4, 1143) * mm});
            skArc(sketch, "E51.4", {"start": v(-3505.2, 1143) * mm, "mid": v(-3415.4, 1180.2) * mm, "end": v(-3378.2, 1270) * mm});
            skArc(sketch, "E51.5", {"start": v(-1473.2, 4775.2) * mm, "mid": v(-1510.4, 4865) * mm, "end": v(-1600.2, 4902.2) * mm});
            skLineSegment(sketch, "E51.6", {"start": v(-1473.2, 4775.2) * mm, "end": v(-1473.2, 4064) * mm});
            skArc(sketch, "E51.7", {"start": v(-1600.2, 3937) * mm, "mid": v(-1510.4, 3974.2) * mm, "end": v(-1473.2, 4064) * mm});
            skLineSegment(sketch, "E52", {"start": v(-3378.2, 1270) * mm, "end": v(-3378.2, 1295.4) * mm});
            skLineSegment(sketch, "E53", {"start": v(-3378.2, 1295.4) * mm, "end": v(-4140.2, 1295.4) * mm});
            skLineSegment(sketch, "E54", {"start": v(-4140.2, 1295.4) * mm, "end": v(-4140.2, 4572) * mm});
            skLineSegment(sketch, "E55", {"start": v(-4013.2, 4699) * mm, "end": v(-1625.6, 4699) * mm});
            skLineSegment(sketch, "E56", {"start": v(-1625.6, 4699) * mm, "end": v(-1625.6, 3937) * mm});
            skLineSegment(sketch, "E57", {"start": v(-1625.6, 3937) * mm, "end": v(-1600.2, 3937) * mm});
            skPoint(sketch, "E58.visualSharp", {"position": v(-4343.4, 4902.2) * mm});
            skArc(sketch, "E58.filletArc", {"start": v(-4216.4, 4902.2) * mm, "mid": v(-4306.2, 4865) * mm, "end": v(-4343.4, 4775.2) * mm});
            skPoint(sketch, "E59.visualSharp", {"position": v(-4140.2, 4699) * mm});
            skArc(sketch, "E59.filletArc", {"start": v(-4013.2, 4699) * mm, "mid": v(-4103, 4661.8) * mm, "end": v(-4140.2, 4572) * mm});
            skSolve(sketch);
        }
        {
            var Q0;
            Q0=makeQuery(id+"F10.imprint","IMPRINT",FACE,{"disambiguationData":[TD([[makeQuery(id+"F10.imprint","IMPRINT",EDGE,{"derivedFrom":sQuery(id+"F10.wireOp",EDGE,"E51.0")}),-1.0]])]});
            extrude(context, id + "F11", {"entities" : qUnion([Q0]), "operationType" : NewBodyOperationType.ADD, "depth" : 101.6 * mm});
        }
        {
            var Q0;
            Q0=makeQuery(id+"F11.opExtrude","CAP_FACE",FACE,{"disambiguationData":[OSD([sQuery(id+"F10.wireOp",EDGE,"E51.0"),sQuery(id+"F10.wireOp",EDGE,"E51.1"),sQuery(id+"F10.wireOp",EDGE,"E51.2"),sQuery(id+"F10.wireOp",EDGE,"E51.3"),sQuery(id+"F10.wireOp",EDGE,"E51.4"),sQuery(id+"F10.wireOp",EDGE,"E51.5"),sQuery(id+"F10.wireOp",EDGE,"E51.6"),sQuery(id+"F10.wireOp",EDGE,"E51.7"),sQuery(id+"F10.wireOp",EDGE,"E52"),sQuery(id+"F10.wireOp",EDGE,"E53"),sQuery(id+"F10.wireOp",EDGE,"E54"),sQuery(id+"F10.wireOp",EDGE,"E55"),sQuery(id+"F10.wireOp",EDGE,"E56"),sQuery(id+"F10.wireOp",EDGE,"E57")])],"isStart":false});
            var sketch = newSketch(context, id + "F12", { "sketchPlane" : qUnion([Q0])});
            skLineSegment(sketch, "E60.0", {"start": v(-4013.2, 4699) * mm, "end": v(-1625.6, 4699) * mm});
            skArc(sketch, "E60.1", {"start": v(-4013.2, 4699) * mm, "mid": v(-4103, 4661.8) * mm, "end": v(-4140.2, 4572) * mm});
            skLineSegment(sketch, "E60.2", {"start": v(-4216.4, 4902.2) * mm, "end": v(-1600.2, 4902.2) * mm});
            skLineSegment(sketch, "E60.3", {"start": v(-4140.2, 1295.4) * mm, "end": v(-4140.2, 4572) * mm});
            skArc(sketch, "E60.4", {"start": v(-4216.4, 4902.2) * mm, "mid": v(-4306.2, 4865) * mm, "end": v(-4343.4, 4775.2) * mm});
            skLineSegment(sketch, "E60.5", {"start": v(-4343.4, 4775.2) * mm, "end": v(-4343.4, 1270) * mm});
            skArc(sketch, "E60.6", {"start": v(-1473.2, 4775.2) * mm, "mid": v(-1510.4, 4865) * mm, "end": v(-1600.2, 4902.2) * mm});
            skArc(sketch, "E60.7", {"start": v(-4343.4, 1270) * mm, "mid": v(-4306.2, 1180.2) * mm, "end": v(-4216.4, 1143) * mm});
            skLineSegment(sketch, "E61", {"start": v(-4140.2, 1295.4) * mm, "end": v(-4140.2, 1143) * mm});
            skLineSegment(sketch, "E62", {"start": v(-4140.2, 1143) * mm, "end": v(-4216.4, 1143) * mm});
            skLineSegment(sketch, "E63", {"start": v(-1625.6, 4699) * mm, "end": v(-1473.2, 4699) * mm});
            skLineSegment(sketch, "E64", {"start": v(-1473.2, 4699) * mm, "end": v(-1473.2, 4775.2) * mm});
            skSolve(sketch);
        }
        {
            var Q0;
            Q0 = qSketchRegion(id + "F12", true);
            extrude(context, id + "F13", {"entities" : qUnion([Q0]), "operationType" : NewBodyOperationType.ADD, "depth" : 304.8 * mm});
        }
        {
            var Q0;
            Q0=makeQuery(id+"F7.opExtrude","CAP_FACE",FACE,{"disambiguationData":[OSD([sQuery(id+"F6.wireOp",EDGE,"E42.bottom"),sQuery(id+"F6.wireOp",EDGE,"E42.top"),sQuery(id+"F6.wireOp",EDGE,"E42.left"),sQuery(id+"F6.wireOp",EDGE,"E42.right")])],"isStart":true});
            var sketch = newSketch(context, id + "F14", { "sketchPlane" : qUnion([Q0])});
            skLineSegment(sketch, "E65.bottom", {"start": v(-508, 3098.8) * mm, "end": v(-50.8, 3098.8) * mm});
            skLineSegment(sketch, "E65.top", {"start": v(-508, 2082.8) * mm, "end": v(-50.8, 2082.8) * mm});
            skLineSegment(sketch, "E65.left", {"start": v(-508, 3098.8) * mm, "end": v(-508, 2082.8) * mm});
            skLineSegment(sketch, "E65.right", {"start": v(-50.8, 3098.8) * mm, "end": v(-50.8, 2082.8) * mm});
            skSolve(sketch);
        }
        {
            var Q0;
            Q0 = qSketchRegion(id + "F14", true);
            extrude(context, id + "F15", {"entities" : qUnion([Q0]), "depth" : 1016 * mm});
        }
        {
            var Q0;
            Q0=makeQuery(id+"F15.opExtrude","CAP_FACE",FACE,{"disambiguationData":[OSD([sQuery(id+"F14.wireOp",EDGE,"E65.bottom"),sQuery(id+"F14.wireOp",EDGE,"E65.top"),sQuery(id+"F14.wireOp",EDGE,"E65.left"),sQuery(id+"F14.wireOp",EDGE,"E65.right")])],"isStart":false});
            var sketch = newSketch(context, id + "F16", { "sketchPlane" : qUnion([Q0])});
            skPoint(sketch, "E66.firstSnap0", {"position": v(-279.4, 3098.8) * mm});
            skLineSegment(sketch, "E66.bottom", {"start": v(-279.4, 2946.4) * mm, "end": v(-203.2, 2946.4) * mm});
            skLineSegment(sketch, "E66.top", {"start": v(-279.4, 2235.2) * mm, "end": v(-203.2, 2235.2) * mm});
            skLineSegment(sketch, "E66.left", {"start": v(-279.4, 2946.4) * mm, "end": v(-279.4, 2235.2) * mm});
            skLineSegment(sketch, "E66.right", {"start": v(-203.2, 2946.4) * mm, "end": v(-203.2, 2235.2) * mm});
            skLineSegment(sketch, "E67", {"start": v(-50.8, 2590.8) * mm, "end": v(-141.95, 2590.8) * mm, "construction": true});
            skSolve(sketch);
        }
        {
            var Q0;
            Q0 = qSketchRegion(id + "F16", true);
            extrude(context, id + "F17", {"entities" : qUnion([Q0]), "depth" : 762 * mm});
        }
        {
            var Q0;
            Q0=makeQuery(id+"F7.opExtrude","CAP_FACE",FACE,{"disambiguationData":[OSD([sQuery(id+"F6.wireOp",EDGE,"E42.bottom"),sQuery(id+"F6.wireOp",EDGE,"E42.top"),sQuery(id+"F6.wireOp",EDGE,"E42.left"),sQuery(id+"F6.wireOp",EDGE,"E42.right")])],"isStart":true});
            var sketch = newSketch(context, id + "F18", { "sketchPlane" : qUnion([Q0])});
            skLineSegment(sketch, "E68.bottom", {"start": v(4165.6, 2654.3) * mm, "end": v(2032, 2654.3) * mm});
            skLineSegment(sketch, "E68.top", {"start": v(4165.6, 749.3) * mm, "end": v(2032, 749.3) * mm});
            skLineSegment(sketch, "E68.left", {"start": v(4165.6, 2654.3) * mm, "end": v(4165.6, 749.3) * mm});
            skLineSegment(sketch, "E68.right", {"start": v(2032, 2654.3) * mm, "end": v(2032, 749.3) * mm});
            skLineSegment(sketch, "E69.0", {"start": v(4216.4, 3632.2) * mm, "end": v(4216.4, -228.6) * mm});
            skLineSegment(sketch, "E70", {"start": v(4216.4, 1701.8) * mm, "end": v(3827.83, 1701.8) * mm, "construction": true});
            skPoint(sketch, "E70.endSnap0", {"position": v(4216.4, 1701.8) * mm});
            skSolve(sketch);
        }
        {
            var Q0;
            Q0=makeQuery(id+"F18.imprint","IMPRINT",FACE,{"disambiguationData":[TD([[makeQuery(id+"F18.imprint","IMPRINT",EDGE,{"derivedFrom":sQuery(id+"F18.wireOp",EDGE,"E68.bottom")}),1.0]])]});
            extrude(context, id + "F19", {"entities" : qUnion([Q0]), "depth" : 609.6 * mm});
        }
    });
